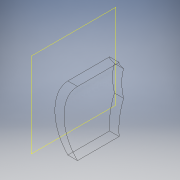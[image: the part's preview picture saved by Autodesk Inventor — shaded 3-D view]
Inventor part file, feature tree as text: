
AUTODESK INVENTOR PART (.ipt)
format: ipt  version: 2018 (Build 220112000, 112)  size: 125,952 bytes
history: native  units: mm
features: extrude x4, sketch x4, plane x1
ambient origin geometry x8: Origin, YZ Plane, XZ Plane, XY Plane, X Axis, Y Axis, Z Axis, Center Point
bodies: Solid1 (feature_tree)
feature tree (9):
  extrude  "Extrusion1"  Depth=12.0mm TaperAngle=0.0deg
  plane  "Work Plane1"
  sketch  "Sketch2"  dims[d8=-10.0mm d9=10.0mm]
  extrude  "Extrusion2"  Depth=10.0mm
  extrude  "Extrusion7"  Depth=4.0mm
  extrude  "Extrusion9"  Depth=7.0mm
  sketch  "Sketch1"  dims[d0=14.0mm d1=12.0mm d2=0.0mm]
  sketch  "Sketch7"  dims[d10=6.5mm d12=4.0mm]
  sketch  "Sketch9"  dims[d14=3.0mm d15=3.0mm d16=10.0mm d17=0.0mm d24=2.0mm d34=10.0mm d35=0.0mm d40=7.0mm d43=0.0mm d44=0.0mm]
